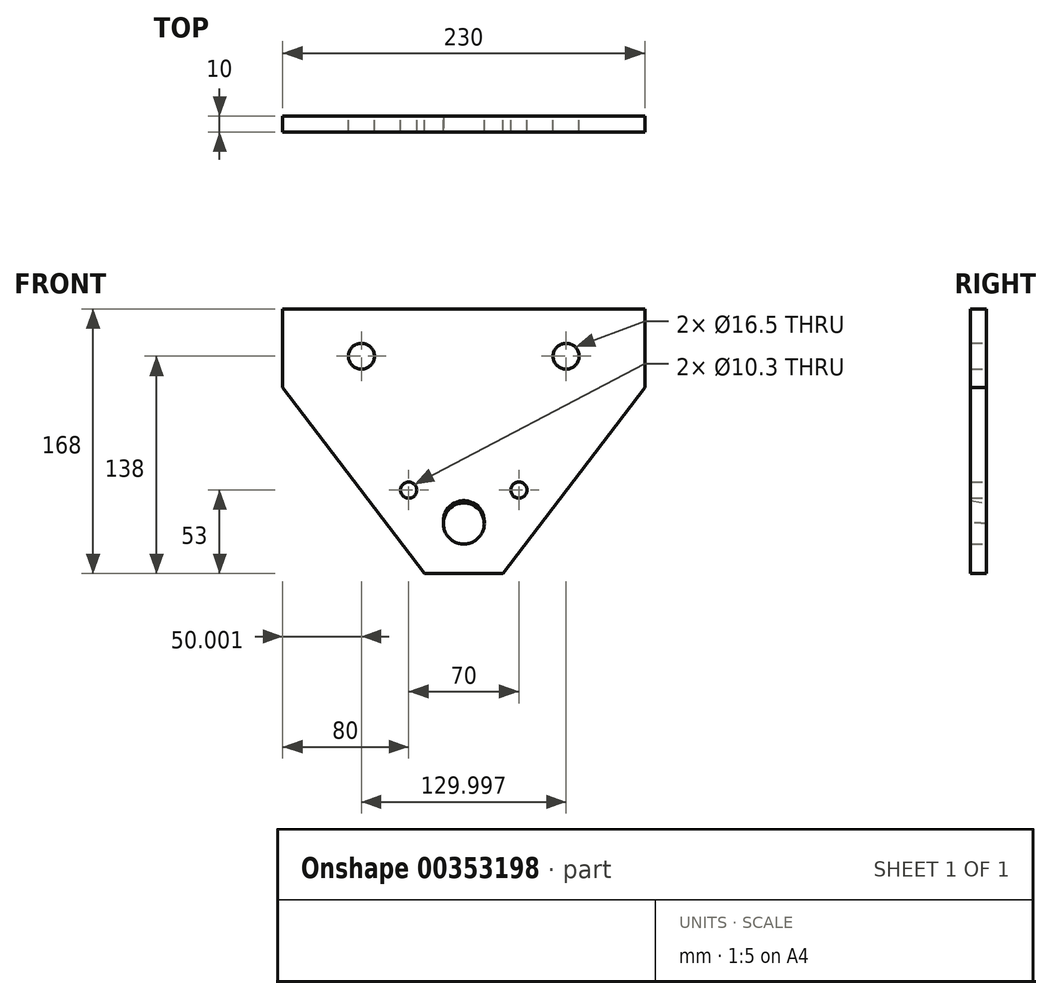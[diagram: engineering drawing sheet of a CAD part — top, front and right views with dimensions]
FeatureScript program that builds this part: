
annotation { "Feature Type Name" : "Feature", "Feature Type Description" : "" }
export const myFeature = defineFeature(function(context is Context, id is Id, definition is map)
    precondition{}
    {
        {
            var Q0;
            Q0=qCreatedBy(makeId("Front.planeOp"),FACE);
            var sketch = newSketch(context, id + "F0", { "sketchPlane" : qUnion([Q0])});
            skLineSegment(sketch, "E0.bottom", {"start": v(115, 30) * mm, "end": v(-115, 30) * mm});
            skLineSegment(sketch, "E0.left", {"start": v(115, 30) * mm, "end": v(115, -20) * mm});
            skPoint(sketch, "E0.middle", {"position": v(0, 0) * mm});
            skLineSegment(sketch, "E1", {"start": v(-25, -138) * mm, "end": v(25, -138) * mm});
            skLineSegment(sketch, "E2", {"start": v(25, -138) * mm, "end": v(115, -20) * mm});
            skCircle(sketch, "E3", {"center": v(65, 0) * mm, "radius": 8.25 * mm});
            skCircle(sketch, "E4", {"center": v(0, -106.33) * mm, "radius": 13 * mm});
            skCircle(sketch, "E5", {"center": v(35, -85) * mm, "radius": 5.15 * mm});
            skCircle(sketch, "E6.MirrorC", {"center": v(-65, 0) * mm, "radius": 8.25 * mm});
            skCircle(sketch, "E7.MirrorC", {"center": v(-35, -85) * mm, "radius": 5.15 * mm});
            skLineSegment(sketch, "E8.MirrorCS", {"start": v(-115, 30) * mm, "end": v(-115, -20) * mm});
            skPoint(sketch, "E9.start.orphan", {"position": v(-115, -30) * mm});
            skLineSegment(sketch, "E10.MirrorCS", {"start": v(-25, -138) * mm, "end": v(-115, -20) * mm});
            skLineSegment(sketch, "E11", {"start": v(-25, -106.33) * mm, "end": v(30.68, -106.33) * mm, "construction": true});
            skSolve(sketch);
        }
        {
            var Q0;
            Q0=makeQuery(id+"F0.imprint","IMPRINT",FACE,{"disambiguationData":[TD([[makeQuery(id+"F0.imprint","IMPRINT",EDGE,{"derivedFrom":sQuery(id+"F0.wireOp",EDGE,"E0.bottom")}),1.0]])]});
            extrude(context, id + "F1", {"entities" : qUnion([Q0]), "depth" : 10 * mm});
        }
        {
            var Q0;
            Q0=sQuery(id+"F0.wireOp",EDGE,"E11");
            cPlane(context, id + "F2", {"entities" : qUnion([Q0]), "cplaneType" : CPlaneType.LINE_ANGLE, "offset" : 25 * mm, "angle" : 8.5 * degree, "oppositeDirection" : true, "width" : 150 * mm, "height" : 150 * mm});
        }
        {
            var Q0;
            Q0=qCreatedBy(id+"F2.planeOp",FACE);
            var sketch = newSketch(context, id + "F3", { "sketchPlane" : qUnion([Q0])});
            skPoint(sketch, "E12.0", {"position": v(0, -105.16) * mm});
            skCircle(sketch, "E13", {"center": v(0, -105.16) * mm, "radius": 13 * mm});
            skSolve(sketch);
        }
        {
            var Q0;
            Q0=makeQuery(id+"F3.imprint","IMPRINT",FACE,{"disambiguationData":[TD([[makeQuery(id+"F3.imprint","IMPRINT",EDGE,{"derivedFrom":sQuery(id+"F3.wireOp",EDGE,"E13")}),1.0]])]});
            extrude(context, id + "F4", {"entities" : qUnion([Q0]), "operationType" : NewBodyOperationType.REMOVE, "endBound" : BoundingType.THROUGH_ALL, "oppositeDirection" : true, "depth" : 25 * mm});
        }
    });
